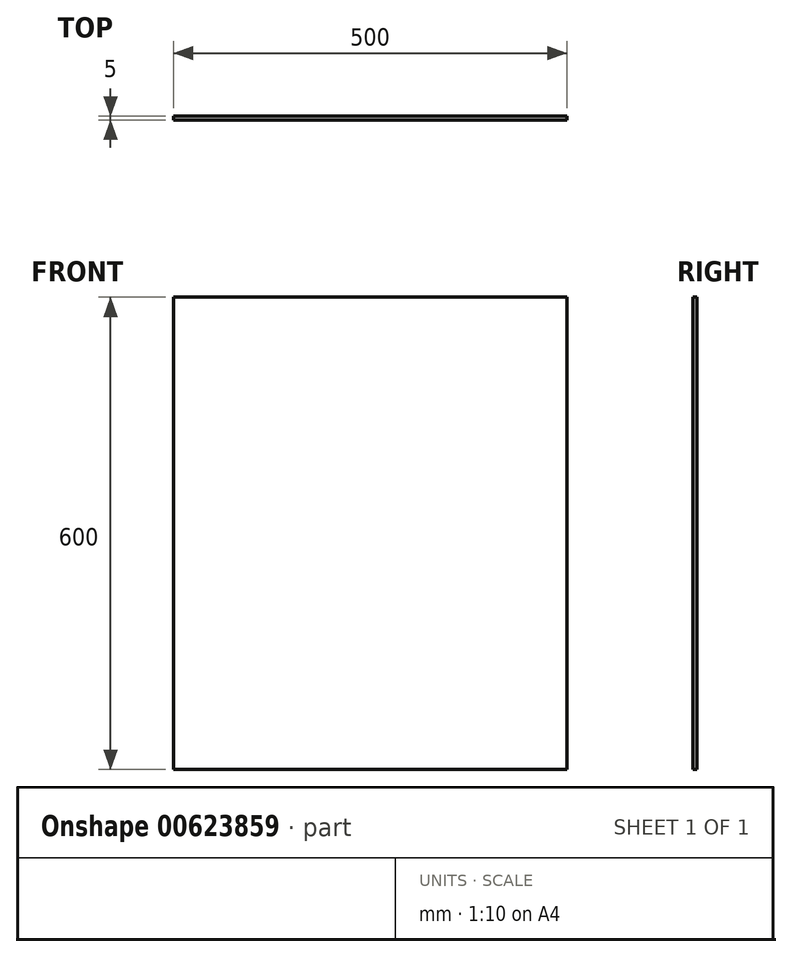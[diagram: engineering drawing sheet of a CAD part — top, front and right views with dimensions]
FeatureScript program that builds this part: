
annotation { "Feature Type Name" : "Feature", "Feature Type Description" : "" }
export const myFeature = defineFeature(function(context is Context, id is Id, definition is map)
    precondition{}
    {
        {
            var Q0;
            Q0=qCreatedBy(makeId("Front.planeOp"),FACE);
            var sketch = newSketch(context, id + "F0", { "sketchPlane" : qUnion([Q0])});
            skLineSegment(sketch, "E0.bottom", {"start": v(0, 0) * mm, "end": v(500, 0) * mm});
            skLineSegment(sketch, "E0.top", {"start": v(0, 600) * mm, "end": v(500, 600) * mm});
            skLineSegment(sketch, "E0.left", {"start": v(0, 0) * mm, "end": v(0, 600) * mm});
            skLineSegment(sketch, "E0.right", {"start": v(500, 0) * mm, "end": v(500, 600) * mm});
            skSolve(sketch);
        }
        {
            var Q0;
            Q0 = qSketchRegion(id + "F0", true);
            extrude(context, id + "F1", {"entities" : qUnion([Q0]), "depth" : 5 * mm, "offsetDistance" : 25 * mm});
        }
    });
